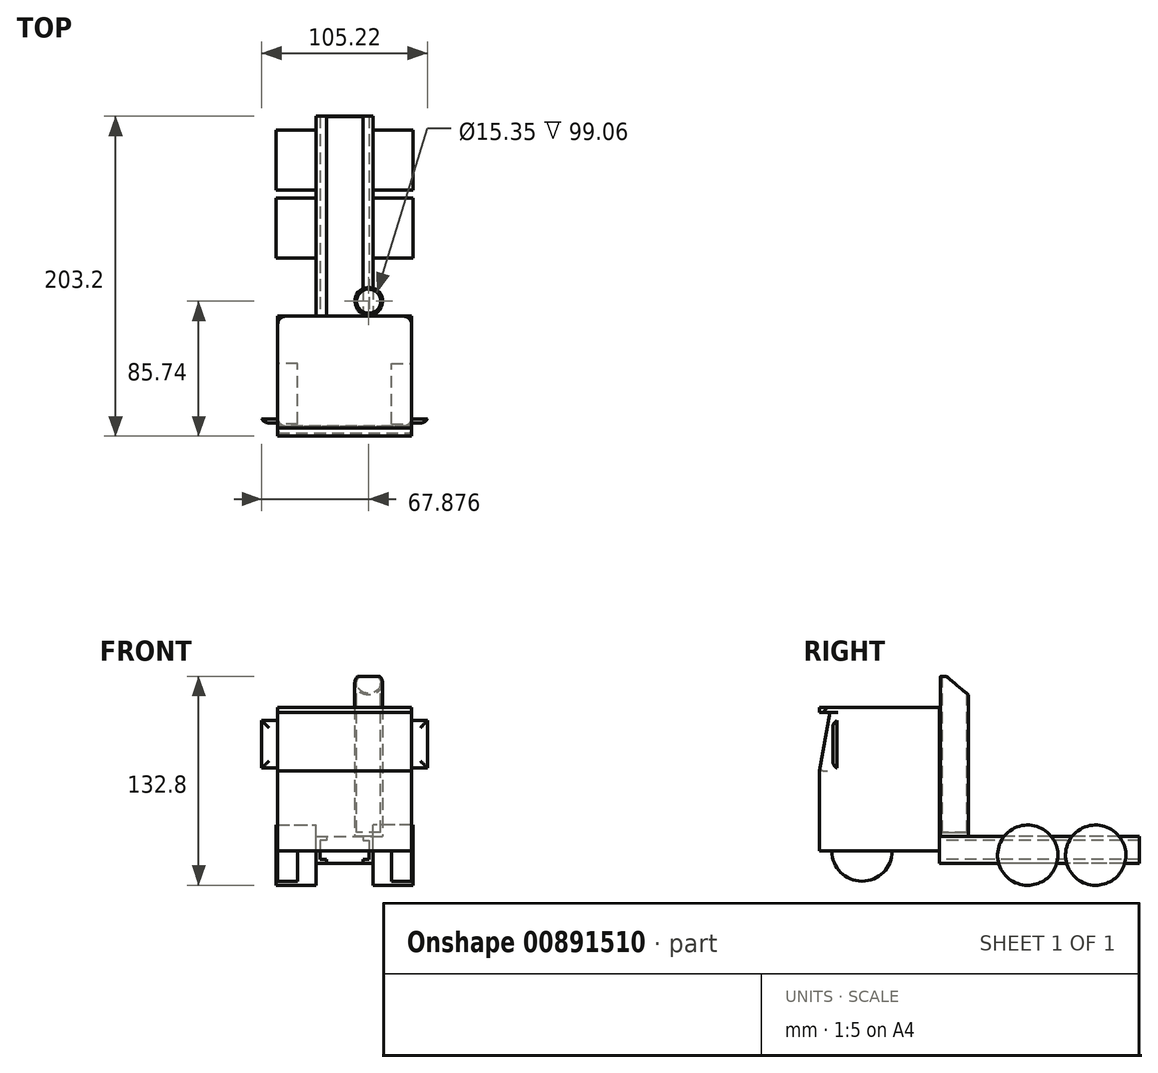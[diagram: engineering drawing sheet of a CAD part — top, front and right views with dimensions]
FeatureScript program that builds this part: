
annotation { "Feature Type Name" : "Feature", "Feature Type Description" : "" }
export const myFeature = defineFeature(function(context is Context, id is Id, definition is map)
    precondition{}
    {
        {
            var Q0;
            Q0=qCreatedBy(makeId("Front.planeOp"),FACE);
            var sketch = newSketch(context, id + "F0", { "sketchPlane" : qUnion([Q0])});
            skLineSegment(sketch, "E0.bottom", {"start": v(-42.45, 45.62) * mm, "end": v(42.45, 45.62) * mm});
            skLineSegment(sketch, "E0.top", {"start": v(-42.45, -45.62) * mm, "end": v(42.45, -45.62) * mm});
            skLineSegment(sketch, "E0.left", {"start": v(-42.45, 45.62) * mm, "end": v(-42.45, -45.62) * mm});
            skLineSegment(sketch, "E0.right", {"start": v(42.45, 45.62) * mm, "end": v(42.45, -45.62) * mm});
            skPoint(sketch, "E0.middle", {"position": v(0, 0) * mm});
            skSolve(sketch);
        }
        {
            var Q0;
            Q0 = qSketchRegion(id + "F0", true);
            extrude(context, id + "F1", {"entities" : qUnion([Q0]), "endBound" : BoundingType.SYMMETRIC, "depth" : 76.2 * mm, "offsetDistance" : 25.4 * mm});
        }
        {
            var Q0;
            Q0=qCreatedBy(makeId("Right.planeOp"),FACE);
            var sketch = newSketch(context, id + "F2", { "sketchPlane" : qUnion([Q0])});
            skLineSegment(sketch, "E1", {"start": v(-38.13, 5.15) * mm, "end": v(-31.62, 42.6) * mm});
            skLineSegment(sketch, "E2", {"start": v(-31.62, 42.6) * mm, "end": v(-38.95, 42.6) * mm});
            skLineSegment(sketch, "E3", {"start": v(-38.95, 42.6) * mm, "end": v(-38.13, 5.15) * mm});
            skSolve(sketch);
        }
        {
            var Q0;
            Q0 = qSketchRegion(id + "F2", true);
            extrude(context, id + "F3", {"entities" : qUnion([Q0]), "operationType" : NewBodyOperationType.REMOVE, "endBound" : BoundingType.THROUGH_ALL, "oppositeDirection" : true, "depth" : 25.4 * mm, "offsetDistance" : 25.4 * mm, "hasSecondDirection" : true, "secondDirectionBound" : SecondDirectionBoundingType.THROUGH_ALL, "secondDirectionOppositeDirection" : false, "secondDirectionDepth" : 25.4 * mm});
        }
        {
            var Q0;
            Q0=makeQuery(id+"F1.opExtrude","SWEPT_FACE",FACE,{"disambiguationData":[OSD([sQuery(id+"F0.wireOp",EDGE,"E0.right")])]});
            var sketch = newSketch(context, id + "F4", { "sketchPlane" : qUnion([Q0])});
            skCircle(sketch, "E4", {"center": v(-11.18, -45.62) * mm, "radius": 19.15 * mm});
            skSolve(sketch);
        }
        {
            var Q0;
            Q0 = qSketchRegion(id + "F4", true);
            extrude(context, id + "F5", {"entities" : qUnion([Q0]), "operationType" : NewBodyOperationType.ADD, "oppositeDirection" : true, "depth" : 12.7 * mm, "offsetDistance" : 25.4 * mm});
        }
        {
            var Q0;
            Q0=makeQuery(id+"F1.opExtrude","SWEPT_BODY",BODY,{"disambiguationData":[OSD([sQuery(id+"F0.wireOp",EDGE,"E0.bottom"),sQuery(id+"F0.wireOp",EDGE,"E0.top"),sQuery(id+"F0.wireOp",EDGE,"E0.left"),sQuery(id+"F0.wireOp",EDGE,"E0.right")])]});
            var Q1;
            Q1=qCreatedBy(makeId("Right.planeOp"),FACE);
            mirror(context, id + "F6", {"entities" : qUnion([Q0]), "mirrorPlane" : qUnion([Q1])});
        }
        {
            var Q0;
            Q0=makeQuery(id+"F1.opExtrude","CAP_FACE",FACE,{"disambiguationData":[OSD([sQuery(id+"F0.wireOp",EDGE,"E0.bottom"),sQuery(id+"F0.wireOp",EDGE,"E0.top"),sQuery(id+"F0.wireOp",EDGE,"E0.left"),sQuery(id+"F0.wireOp",EDGE,"E0.right")])],"isStart":true});
            var sketch = newSketch(context, id + "F7", { "sketchPlane" : qUnion([Q0])});
            skLineSegment(sketch, "E5", {"start": v(-11.57, -53.28) * mm, "end": v(-18.18, -53.28) * mm});
            skLineSegment(sketch, "E6", {"start": v(-18.18, -53.28) * mm, "end": v(-18.18, -36.14) * mm});
            skLineSegment(sketch, "E7", {"start": v(-18.18, -36.14) * mm, "end": v(-11.57, -36.14) * mm});
            skLineSegment(sketch, "E8", {"start": v(-11.57, -36.14) * mm, "end": v(-11.57, -38.68) * mm});
            skLineSegment(sketch, "E9", {"start": v(-11.57, -38.68) * mm, "end": v(-15.64, -38.68) * mm});
            skLineSegment(sketch, "E10", {"start": v(-15.64, -38.68) * mm, "end": v(-15.64, -50.74) * mm});
            skLineSegment(sketch, "E11", {"start": v(-15.64, -50.74) * mm, "end": v(-11.57, -50.74) * mm});
            skLineSegment(sketch, "E12", {"start": v(-11.57, -50.74) * mm, "end": v(-11.57, -53.28) * mm});
            skSolve(sketch);
        }
        {
            var Q0;
            Q0 = qSketchRegion(id + "F7", true);
            extrude(context, id + "F8", {"entities" : qUnion([Q0]), "depth" : 127 * mm, "offsetDistance" : 25.4 * mm});
        }
        {
            var Q0;
            Q0=makeQuery(id+"F8.opExtrude","SWEPT_BODY",BODY,{"disambiguationData":[OSD([sQuery(id+"F7.wireOp",EDGE,"E5"),sQuery(id+"F7.wireOp",EDGE,"E6"),sQuery(id+"F7.wireOp",EDGE,"E7"),sQuery(id+"F7.wireOp",EDGE,"E8"),sQuery(id+"F7.wireOp",EDGE,"E9"),sQuery(id+"F7.wireOp",EDGE,"E10"),sQuery(id+"F7.wireOp",EDGE,"E11"),sQuery(id+"F7.wireOp",EDGE,"E12")])]});
            var Q1;
            Q1=qCreatedBy(makeId("Right.planeOp"),FACE);
            mirror(context, id + "F9", {"entities" : qUnion([Q0]), "mirrorPlane" : qUnion([Q1])});
        }
        {
            var Q0;
            Q0=makeQuery(id+"F8.opExtrude","SWEPT_FACE",FACE,{"disambiguationData":[OSD([sQuery(id+"F7.wireOp",EDGE,"E6")])]});
            var sketch = newSketch(context, id + "F10", { "sketchPlane" : qUnion([Q0])});
            skCircle(sketch, "E13", {"center": v(137.27, -48.2) * mm, "radius": 19.15 * mm});
            skCircle(sketch, "E14", {"center": v(94.1, -48.2) * mm, "radius": 19.15 * mm});
            skSolve(sketch);
        }
        {
            var Q0;
            Q0 = qSketchRegion(id + "F10", true);
            extrude(context, id + "F11", {"entities" : qUnion([Q0]), "operationType" : NewBodyOperationType.ADD, "depth" : 25.4 * mm, "offsetDistance" : 25.4 * mm});
        }
        {
            var Q0;
            Q0=makeQuery(id+"F8.opExtrude","SWEPT_BODY",BODY,{"disambiguationData":[OSD([sQuery(id+"F7.wireOp",EDGE,"E5"),sQuery(id+"F7.wireOp",EDGE,"E6"),sQuery(id+"F7.wireOp",EDGE,"E7"),sQuery(id+"F7.wireOp",EDGE,"E8"),sQuery(id+"F7.wireOp",EDGE,"E9"),sQuery(id+"F7.wireOp",EDGE,"E10"),sQuery(id+"F7.wireOp",EDGE,"E11"),sQuery(id+"F7.wireOp",EDGE,"E12")])]});
            var Q1;
            Q1=qCreatedBy(makeId("Right.planeOp"),FACE);
            mirror(context, id + "F12", {"entities" : qUnion([Q0]), "mirrorPlane" : qUnion([Q1])});
        }
        {
            var Q0;
            {var subQ0=sQuery(id+"F0.wireOp",EDGE,"E0.right");var subQ1=sQuery(id+"F0.wireOp",EDGE,"E0.top");Q0=makeQuery(id+"F3.boolean.opBoolean","SPLIT",EDGE,{"disambiguationData":[TD([makeQuery(id+"F1.opExtrude","SWEPT_FACE",FACE,{"disambiguationData":[OSD([subQ1])]})])],"derivedFrom":makeQuery(id+"F1.opExtrude","CAP_EDGE",EDGE,{"disambiguationData":[OSD([subQ0])],"isStart":false})});}
            var Q1;
            Q1=makeQuery(id+"F3.boolean.opBoolean","INTERSECT",EDGE,{"derivedFrom":[makeQuery(id+"F1.opExtrude","SWEPT_FACE",FACE,{"disambiguationData":[OSD([sQuery(id+"F0.wireOp",EDGE,"E0.right")])]}),makeQuery(id+"F3.opExtrude","SWEPT_FACE",FACE,{"disambiguationData":[OSD([sQuery(id+"F2.wireOp",EDGE,"E1")])]})]});
            var Q2;
            {var subQ0=sQuery(id+"F0.wireOp",EDGE,"E0.left");var subQ1=sQuery(id+"F0.wireOp",EDGE,"E0.top");Q2=makeQuery(id+"F3.boolean.opBoolean","SPLIT",EDGE,{"disambiguationData":[TD([makeQuery(id+"F1.opExtrude","SWEPT_FACE",FACE,{"disambiguationData":[OSD([subQ1])]})])],"derivedFrom":makeQuery(id+"F1.opExtrude","CAP_EDGE",EDGE,{"disambiguationData":[OSD([subQ0])],"isStart":false})});}
            var Q3;
            Q3=makeQuery(id+"F3.boolean.opBoolean","INTERSECT",EDGE,{"derivedFrom":[makeQuery(id+"F1.opExtrude","SWEPT_FACE",FACE,{"disambiguationData":[OSD([sQuery(id+"F0.wireOp",EDGE,"E0.left")])]}),makeQuery(id+"F3.opExtrude","SWEPT_FACE",FACE,{"disambiguationData":[OSD([sQuery(id+"F2.wireOp",EDGE,"E1")])]})]});
            var Q4;
            Q4=makeQuery(id+"F1.opExtrude","CAP_EDGE",EDGE,{"disambiguationData":[OSD([sQuery(id+"F0.wireOp",EDGE,"E0.right")])],"isStart":true});
            var Q5;
            Q5=makeQuery(id+"F1.opExtrude","CAP_EDGE",EDGE,{"disambiguationData":[OSD([sQuery(id+"F0.wireOp",EDGE,"E0.left")])],"isStart":true});
            fillet(context, id + "F13", {"entities" : qUnion([Q0, Q1, Q2, Q3, Q4, Q5]), "radius" : 5.08 * mm, "tangentPropagation" : true, "allowEdgeOverflow" : false});
        }
        {
            var Q0;
            Q0=makeQuery(id+"F1.opExtrude","CAP_EDGE",EDGE,{"disambiguationData":[OSD([sQuery(id+"F0.wireOp",EDGE,"E0.bottom")])],"isStart":false});
            chamfer(context, id + "F14", {"entities" : qUnion([Q0]), "width" : 5.08 * mm, "tangentPropagation" : true});
        }
        {
            var Q0;
            Q0=makeQuery(id+"F8.opExtrude","SWEPT_FACE",FACE,{"disambiguationData":[OSD([sQuery(id+"F7.wireOp",EDGE,"E7")])]});
            var sketch = newSketch(context, id + "F15", { "sketchPlane" : qUnion([Q0])});
            skCircle(sketch, "E15", {"center": v(15.27, 47.64) * mm, "radius": 8.86 * mm});
            skSolve(sketch);
        }
        {
            var Q0;
            Q0 = qSketchRegion(id + "F15", true);
            extrude(context, id + "F16", {"entities" : qUnion([Q0]), "operationType" : NewBodyOperationType.ADD, "depth" : 101.6 * mm, "offsetDistance" : 25.4 * mm});
        }
        {
            var Q0;
            Q0=makeQuery(id+"F16.opExtrude","CAP_FACE",FACE,{"disambiguationData":[OSD([sQuery(id+"F15.wireOp",EDGE,"E15")])],"isStart":false});
            var sketch = newSketch(context, id + "F17", { "sketchPlane" : qUnion([Q0])});
            skCircle(sketch, "E16", {"center": v(15.27, 47.64) * mm, "radius": 7.67 * mm});
            skSolve(sketch);
        }
        {
            var Q0;
            Q0 = qSketchRegion(id + "F17", true);
            extrude(context, id + "F18", {"entities" : qUnion([Q0]), "operationType" : NewBodyOperationType.REMOVE, "oppositeDirection" : true, "depth" : 99.06 * mm, "offsetDistance" : 25.4 * mm});
        }
        {
            var Q0;
            Q0=qCreatedBy(makeId("Right.planeOp"),FACE);
            var sketch = newSketch(context, id + "F19", { "sketchPlane" : qUnion([Q0])});
            skLineSegment(sketch, "E17", {"start": v(33.84, 72.48) * mm, "end": v(58.77, 51.66) * mm});
            skLineSegment(sketch, "E18", {"start": v(58.77, 51.66) * mm, "end": v(58.77, 70.78) * mm});
            skLineSegment(sketch, "E19", {"start": v(58.77, 70.78) * mm, "end": v(33.84, 72.48) * mm});
            skSolve(sketch);
        }
        {
            var Q0;
            Q0 = qSketchRegion(id + "F19", true);
            extrude(context, id + "F20", {"entities" : qUnion([Q0]), "operationType" : NewBodyOperationType.REMOVE, "endBound" : BoundingType.THROUGH_ALL, "depth" : 25.4 * mm, "offsetDistance" : 25.4 * mm});
        }
        {
            var Q0;
            Q0=makeQuery(id+"F5.boolean.opBoolean","MERGE",FACE,{"derivedFrom":[makeQuery(id+"F1.opExtrude","SWEPT_FACE",FACE,{"disambiguationData":[OSD([sQuery(id+"F0.wireOp",EDGE,"E0.right")])]}),makeQuery(id+"F5.opExtrude","CAP_FACE",FACE,{"disambiguationData":[OSD([sQuery(id+"F4.wireOp",EDGE,"E4")])],"isStart":true})]});
            var sketch = newSketch(context, id + "F21", { "sketchPlane" : qUnion([Q0])});
            skLineSegment(sketch, "E20.bottom", {"start": v(-29.74, 37.23) * mm, "end": v(-27.1, 37.23) * mm});
            skLineSegment(sketch, "E20.top", {"start": v(-29.74, 7.1) * mm, "end": v(-27.1, 7.1) * mm});
            skLineSegment(sketch, "E20.left", {"start": v(-29.74, 37.23) * mm, "end": v(-29.74, 7.1) * mm});
            skLineSegment(sketch, "E20.right", {"start": v(-27.1, 37.23) * mm, "end": v(-27.1, 7.1) * mm});
            skPoint(sketch, "E20.middle", {"position": v(-28.42, 22.17) * mm});
            skPoint(sketch, "E20.cornerSnap0", {"position": v(-29.74, 23.76) * mm});
            skSolve(sketch);
        }
        {
            var Q0;
            Q0 = qSketchRegion(id + "F21", true);
            extrude(context, id + "F22", {"entities" : qUnion([Q0]), "depth" : 10.16 * mm, "offsetDistance" : 25.4 * mm});
        }
        {
            var Q0;
            Q0=makeQuery(id+"F22.opExtrude","SWEPT_EDGE",EDGE,{"disambiguationData":[OSD([sQuery(id+"F21.wireOp",EDGE,"E20.bottom"),sQuery(id+"F21.wireOp",EDGE,"E20.left")])]});
            var Q1;
            Q1=makeQuery(id+"F22.opExtrude","CAP_EDGE",EDGE,{"disambiguationData":[OSD([sQuery(id+"F21.wireOp",EDGE,"E20.left")])],"isStart":false});
            var Q2;
            Q2=makeQuery(id+"F22.opExtrude","SWEPT_EDGE",EDGE,{"disambiguationData":[OSD([sQuery(id+"F21.wireOp",EDGE,"E20.top"),sQuery(id+"F21.wireOp",EDGE,"E20.left")])]});
            fillet(context, id + "F23", {"entities" : qUnion([Q0, Q1, Q2]), "radius" : 5.08 * mm, "tangentPropagation" : true, "allowEdgeOverflow" : false});
        }
        {
            var Q0;
            Q0=makeQuery(id+"F22.opExtrude","SWEPT_BODY",BODY,{"disambiguationData":[OSD([sQuery(id+"F21.wireOp",EDGE,"E20.bottom"),sQuery(id+"F21.wireOp",EDGE,"E20.top"),sQuery(id+"F21.wireOp",EDGE,"E20.left"),sQuery(id+"F21.wireOp",EDGE,"E20.right")])]});
            var Q1;
            Q1=qCreatedBy(makeId("Right.planeOp"),FACE);
            mirror(context, id + "F24", {"entities" : qUnion([Q0]), "mirrorPlane" : qUnion([Q1])});
        }
        {
            var Q0;
            Q0=makeQuery(id+"F8.opExtrude","CAP_FACE",FACE,{"disambiguationData":[OSD([sQuery(id+"F7.wireOp",EDGE,"E5"),sQuery(id+"F7.wireOp",EDGE,"E6"),sQuery(id+"F7.wireOp",EDGE,"E7"),sQuery(id+"F7.wireOp",EDGE,"E8"),sQuery(id+"F7.wireOp",EDGE,"E9"),sQuery(id+"F7.wireOp",EDGE,"E10"),sQuery(id+"F7.wireOp",EDGE,"E11"),sQuery(id+"F7.wireOp",EDGE,"E12")])],"isStart":false});
            var sketch = newSketch(context, id + "F25", { "sketchPlane" : qUnion([Q0])});
            skLineSegment(sketch, "E21", {"start": v(18.1, -36.15) * mm, "end": v(-18.18, -36.14) * mm});
            skLineSegment(sketch, "E22", {"start": v(-18.18, -36.14) * mm, "end": v(-18.18, -53.28) * mm});
            skLineSegment(sketch, "E23", {"start": v(-18.18, -53.28) * mm, "end": v(18.11, -53.28) * mm});
            skLineSegment(sketch, "E24", {"start": v(18.11, -53.28) * mm, "end": v(18.1, -36.15) * mm});
            skSolve(sketch);
        }
        {
            var Q0;
            Q0 = qSketchRegion(id + "F25", true);
            extrude(context, id + "F26", {"entities" : qUnion([Q0]), "oppositeDirection" : true, "depth" : 0.25 * mm, "offsetDistance" : 25.4 * mm});
        }
    });
